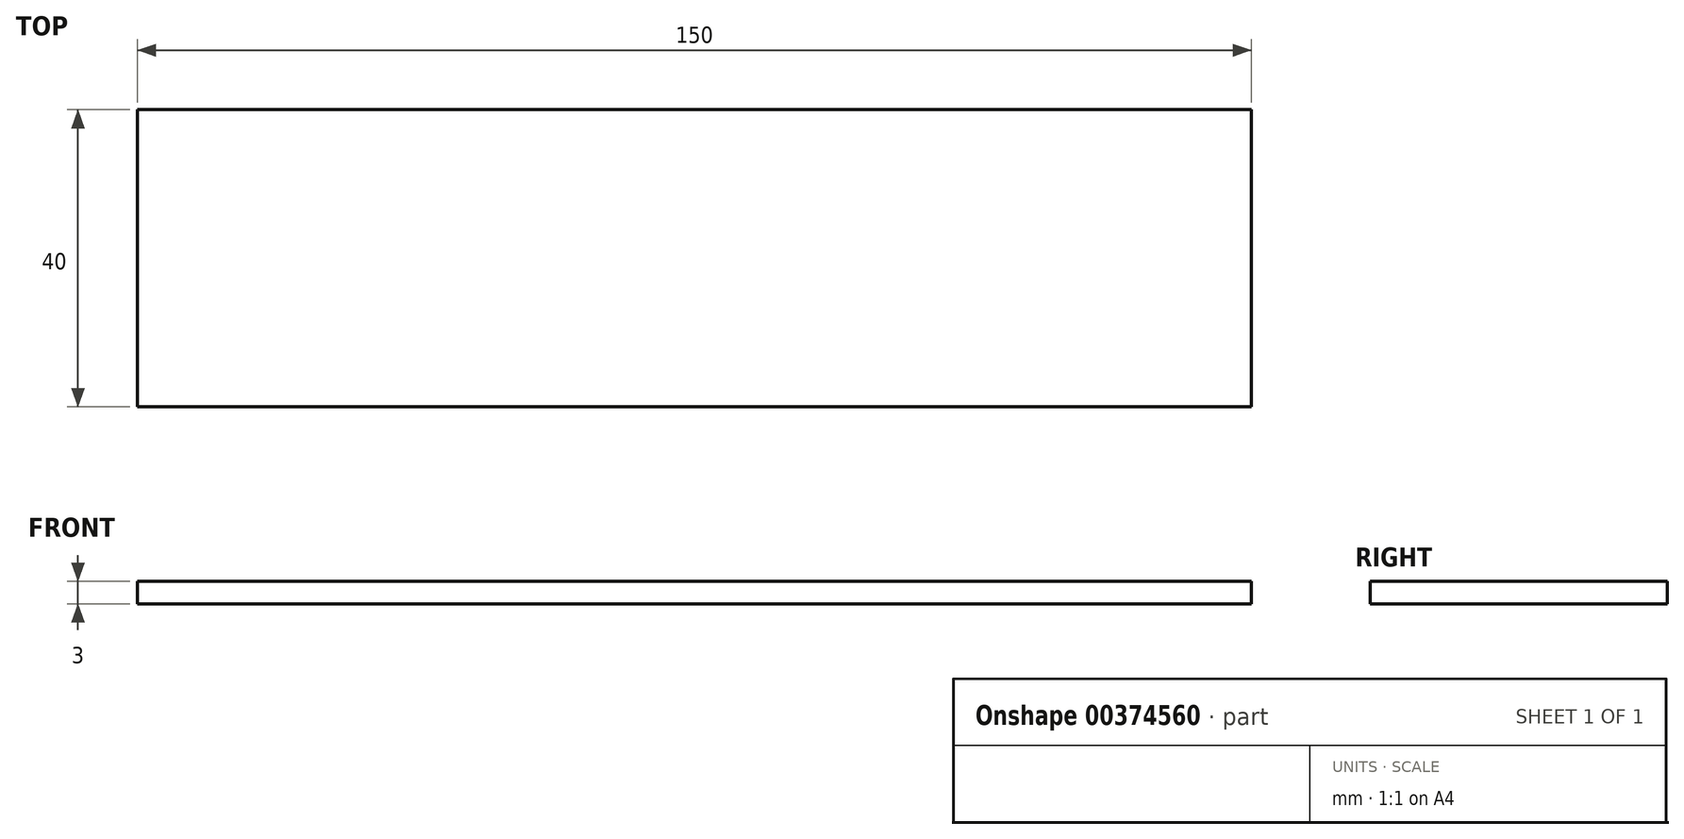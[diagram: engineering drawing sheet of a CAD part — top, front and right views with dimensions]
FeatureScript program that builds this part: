
annotation { "Feature Type Name" : "Feature", "Feature Type Description" : "" }
export const myFeature = defineFeature(function(context is Context, id is Id, definition is map)
    precondition{}
    {
        {
            var Q0;
            Q0=qCreatedBy(makeId("Top.planeOp"),FACE);
            var sketch = newSketch(context, id + "F0", { "sketchPlane" : qUnion([Q0])});
            skLineSegment(sketch, "E0.bottom", {"start": v(-56.64, 19.2) * mm, "end": v(93.36, 19.2) * mm});
            skLineSegment(sketch, "E0.top", {"start": v(-56.64, -20.8) * mm, "end": v(93.36, -20.8) * mm});
            skLineSegment(sketch, "E0.left", {"start": v(-56.64, 19.2) * mm, "end": v(-56.64, -20.8) * mm});
            skLineSegment(sketch, "E0.right", {"start": v(93.36, 19.2) * mm, "end": v(93.36, -20.8) * mm});
            skSolve(sketch);
        }
        {
            var Q0;
            Q0=makeQuery(id+"F0.imprint","IMPRINT",FACE,{"disambiguationData":[TD([[makeQuery(id+"F0.imprint","IMPRINT",EDGE,{"derivedFrom":sQuery(id+"F0.wireOp",EDGE,"E0.bottom")}),-1.0]])]});
            extrude(context, id + "F1", {"entities" : qUnion([Q0]), "depth" : 3 * mm});
        }
    });
